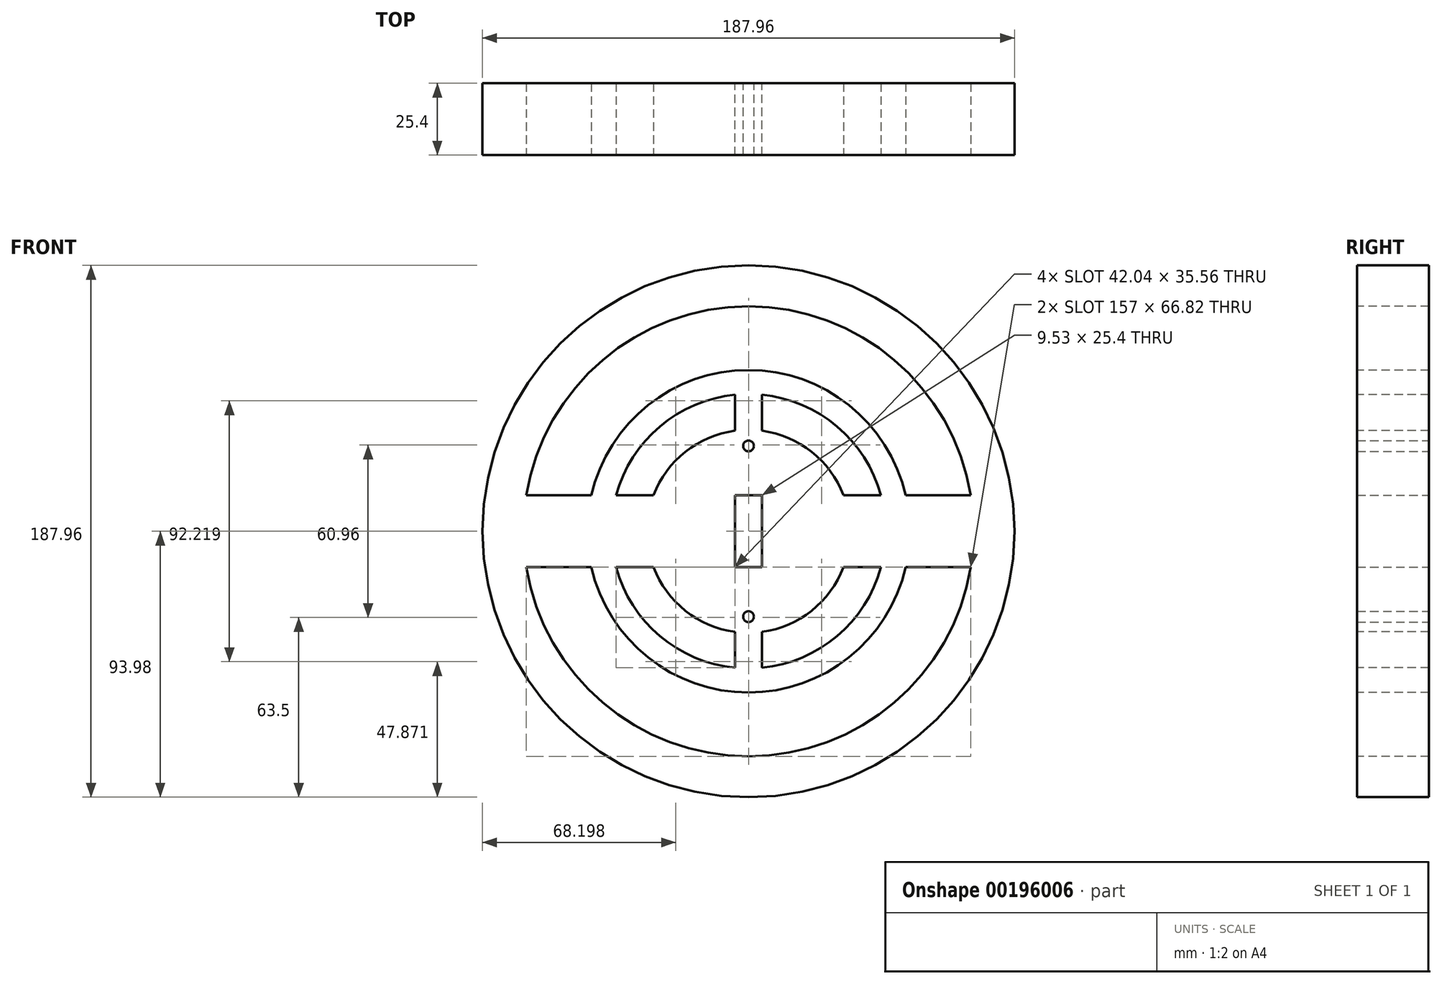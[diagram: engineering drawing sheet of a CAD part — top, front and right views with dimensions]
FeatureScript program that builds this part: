
annotation { "Feature Type Name" : "Feature", "Feature Type Description" : "" }
export const myFeature = defineFeature(function(context is Context, id is Id, definition is map)
    precondition{}
    {
        {
            var Q0;
            Q0=qCreatedBy(makeId("Front.planeOp"),FACE);
            var sketch = newSketch(context, id + "F0", { "sketchPlane" : qUnion([Q0])});
            skCircle(sketch, "E0", {"center": v(0, 0) * mm, "radius": 93.98 * mm});
            skSolve(sketch);
        }
        {
            var Q0;
            Q0=makeQuery(id+"F0.imprint","IMPRINT",FACE,{"disambiguationData":[TD([[makeQuery(id+"F0.imprint","IMPRINT",EDGE,{"derivedFrom":sQuery(id+"F0.wireOp",EDGE,"E0")}),1.0]])]});
            extrude(context, id + "F1", {"entities" : qUnion([Q0]), "depth" : 25.4 * mm});
        }
        {
            var Q0;
            Q0=qCreatedBy(makeId("Front.planeOp"),FACE);
            var sketch = newSketch(context, id + "F2", { "sketchPlane" : qUnion([Q0])});
            skLineSegment(sketch, "E1.bottom", {"start": v(4.76, 12.7) * mm, "end": v(-4.76, 12.7) * mm});
            skLineSegment(sketch, "E1.top", {"start": v(4.76, -12.7) * mm, "end": v(-4.76, -12.7) * mm});
            skLineSegment(sketch, "E1.left", {"start": v(4.76, 12.7) * mm, "end": v(4.76, -12.7) * mm});
            skLineSegment(sketch, "E1.right", {"start": v(-4.76, 12.7) * mm, "end": v(-4.76, -12.7) * mm});
            skPoint(sketch, "E1.middle", {"position": v(0, 0) * mm});
            skCircle(sketch, "E2", {"center": v(0, 30.18) * mm, "radius": 1.9 * mm});
            skPoint(sketch, "E2.centerSnap0", {"position": v(0, 12.7) * mm});
            skCircle(sketch, "E3", {"center": v(0, -30.18) * mm, "radius": 1.9 * mm});
            skPoint(sketch, "E3.centerSnap0", {"position": v(0, -12.7) * mm});
            skSolve(sketch);
        }
        {
            var Q0;
            Q0 = qSketchRegion(id + "F2", true);
            extrude(context, id + "F3", {"entities" : qUnion([Q0]), "operationType" : NewBodyOperationType.REMOVE, "endBound" : BoundingType.THROUGH_ALL, "depth" : 25.4 * mm});
        }
        {
            var Q0;
            Q0=makeQuery(id+"F1.opExtrude","CAP_FACE",FACE,{"disambiguationData":[OSD([sQuery(id+"F0.wireOp",EDGE,"E0")])],"isStart":false});
            var sketch = newSketch(context, id + "F4", { "sketchPlane" : qUnion([Q0])});
            skLineSegment(sketch, "E4", {"start": v(55.56, 12.7) * mm, "end": v(78.5, 12.7) * mm});
            skArc(sketch, "E5", {"start": v(78.5, 12.7) * mm, "mid": v(0, 79.52) * mm, "end": v(-78.5, 12.7) * mm});
            skArc(sketch, "E6", {"start": v(55.56, 12.7) * mm, "mid": v(0, 57) * mm, "end": v(-55.56, 12.7) * mm});
            skLineSegment(sketch, "E7", {"start": v(-78.5, 12.7) * mm, "end": v(-55.56, 12.7) * mm});
            skPoint(sketch, "E8.endSnap0", {"position": v(4.76, 0) * mm});
            skLineSegment(sketch, "E9.MirrorCS", {"start": v(55.56, -12.7) * mm, "end": v(78.5, -12.7) * mm});
            skArc(sketch, "E10.MirrorCS", {"start": v(78.5, -12.7) * mm, "mid": v(0, -79.52) * mm, "end": v(-78.5, -12.7) * mm});
            skArc(sketch, "E11.MirrorCS", {"start": v(55.56, -12.7) * mm, "mid": v(0, -57) * mm, "end": v(-55.56, -12.7) * mm});
            skLineSegment(sketch, "E12.MirrorCS", {"start": v(-78.5, -12.7) * mm, "end": v(-55.56, -12.7) * mm});
            skSolve(sketch);
        }
        {
            var Q0;
            Q0=makeQuery(id+"F4.imprint","IMPRINT",FACE,{"disambiguationData":[TD([[makeQuery(id+"F4.imprint","IMPRINT",EDGE,{"derivedFrom":sQuery(id+"F4.wireOp",EDGE,"E4")}),1.0]])]});
            var Q1;
            Q1=makeQuery(id+"F4.imprint","IMPRINT",FACE,{"disambiguationData":[TD([[makeQuery(id+"F4.imprint","IMPRINT",EDGE,{"derivedFrom":sQuery(id+"F4.wireOp",EDGE,"E9.MirrorCS")}),-1.0]])]});
            extrude(context, id + "F5", {"entities" : qUnion([Q0, Q1]), "operationType" : NewBodyOperationType.REMOVE, "endBound" : BoundingType.THROUGH_ALL, "oppositeDirection" : true, "depth" : 25.4 * mm});
        }
        {
            var Q0;
            Q0=makeQuery(id+"F1.opExtrude","CAP_FACE",FACE,{"disambiguationData":[OSD([sQuery(id+"F0.wireOp",EDGE,"E0")])],"isStart":false});
            var sketch = newSketch(context, id + "F6", { "sketchPlane" : qUnion([Q0])});
            skLineSegment(sketch, "E13", {"start": v(4.76, 35.56) * mm, "end": v(4.76, 48.26) * mm});
            skLineSegment(sketch, "E14", {"start": v(46.8, 12.7) * mm, "end": v(33.55, 12.7) * mm});
            skArc(sketch, "E15", {"start": v(4.76, 48.26) * mm, "mid": v(31.32, 37.03) * mm, "end": v(46.8, 12.7) * mm});
            skPoint(sketch, "E16.orphan", {"position": v(23.35, 0) * mm});
            skArc(sketch, "E17", {"start": v(4.76, 35.56) * mm, "mid": v(22.3, 28.1) * mm, "end": v(33.55, 12.7) * mm});
            skPoint(sketch, "E18.start.orphan", {"position": v(4.76, 22.86) * mm});
            skLineSegment(sketch, "E19.MirrorCS", {"start": v(46.8, -12.7) * mm, "end": v(33.55, -12.7) * mm});
            skArc(sketch, "E20.MirrorCS", {"start": v(4.76, -48.26) * mm, "mid": v(31.32, -37.03) * mm, "end": v(46.8, -12.7) * mm});
            skArc(sketch, "E21.MirrorCS", {"start": v(4.76, -35.56) * mm, "mid": v(22.3, -28.1) * mm, "end": v(33.55, -12.7) * mm});
            skLineSegment(sketch, "E22.MirrorCS", {"start": v(4.76, -35.56) * mm, "end": v(4.76, -48.26) * mm});
            skLineSegment(sketch, "E23.MirrorCS", {"start": v(-4.76, 35.56) * mm, "end": v(-4.76, 48.26) * mm});
            skArc(sketch, "E24.MirrorCS", {"start": v(-4.76, 35.56) * mm, "mid": v(-22.3, 28.1) * mm, "end": v(-33.55, 12.7) * mm});
            skArc(sketch, "E25.MirrorCS", {"start": v(-4.76, 48.26) * mm, "mid": v(-31.32, 37.03) * mm, "end": v(-46.8, 12.7) * mm});
            skLineSegment(sketch, "E26.MirrorCS", {"start": v(-46.8, 12.7) * mm, "end": v(-33.55, 12.7) * mm});
            skLineSegment(sketch, "E27.MirrorCS", {"start": v(-4.76, -35.56) * mm, "end": v(-4.76, -48.26) * mm});
            skArc(sketch, "E28.MirrorCS", {"start": v(-4.76, -35.56) * mm, "mid": v(-22.3, -28.1) * mm, "end": v(-33.55, -12.7) * mm});
            skArc(sketch, "E29.MirrorCS", {"start": v(-4.76, -48.26) * mm, "mid": v(-31.32, -37.03) * mm, "end": v(-46.8, -12.7) * mm});
            skLineSegment(sketch, "E30.MirrorCS", {"start": v(-46.8, -12.7) * mm, "end": v(-33.55, -12.7) * mm});
            skSolve(sketch);
        }
        {
            var Q0;
            Q0=makeQuery(id+"F6.imprint","IMPRINT",FACE,{"disambiguationData":[TD([[makeQuery(id+"F6.imprint","IMPRINT",EDGE,{"derivedFrom":sQuery(id+"F6.wireOp",EDGE,"E23.MirrorCS")}),1.0]])]});
            var Q1;
            Q1=makeQuery(id+"F6.imprint","IMPRINT",FACE,{"disambiguationData":[TD([[makeQuery(id+"F6.imprint","IMPRINT",EDGE,{"derivedFrom":sQuery(id+"F6.wireOp",EDGE,"E13")}),-1.0]])]});
            var Q2;
            Q2=makeQuery(id+"F6.imprint","IMPRINT",FACE,{"disambiguationData":[TD([[makeQuery(id+"F6.imprint","IMPRINT",EDGE,{"derivedFrom":sQuery(id+"F6.wireOp",EDGE,"E19.MirrorCS")}),1.0]])]});
            var Q3;
            Q3=makeQuery(id+"F6.imprint","IMPRINT",FACE,{"disambiguationData":[TD([[makeQuery(id+"F6.imprint","IMPRINT",EDGE,{"derivedFrom":sQuery(id+"F6.wireOp",EDGE,"E27.MirrorCS")}),-1.0]])]});
            extrude(context, id + "F7", {"entities" : qUnion([Q0, Q1, Q2, Q3]), "operationType" : NewBodyOperationType.REMOVE, "endBound" : BoundingType.THROUGH_ALL, "oppositeDirection" : true, "depth" : 25.4 * mm});
        }
    });
